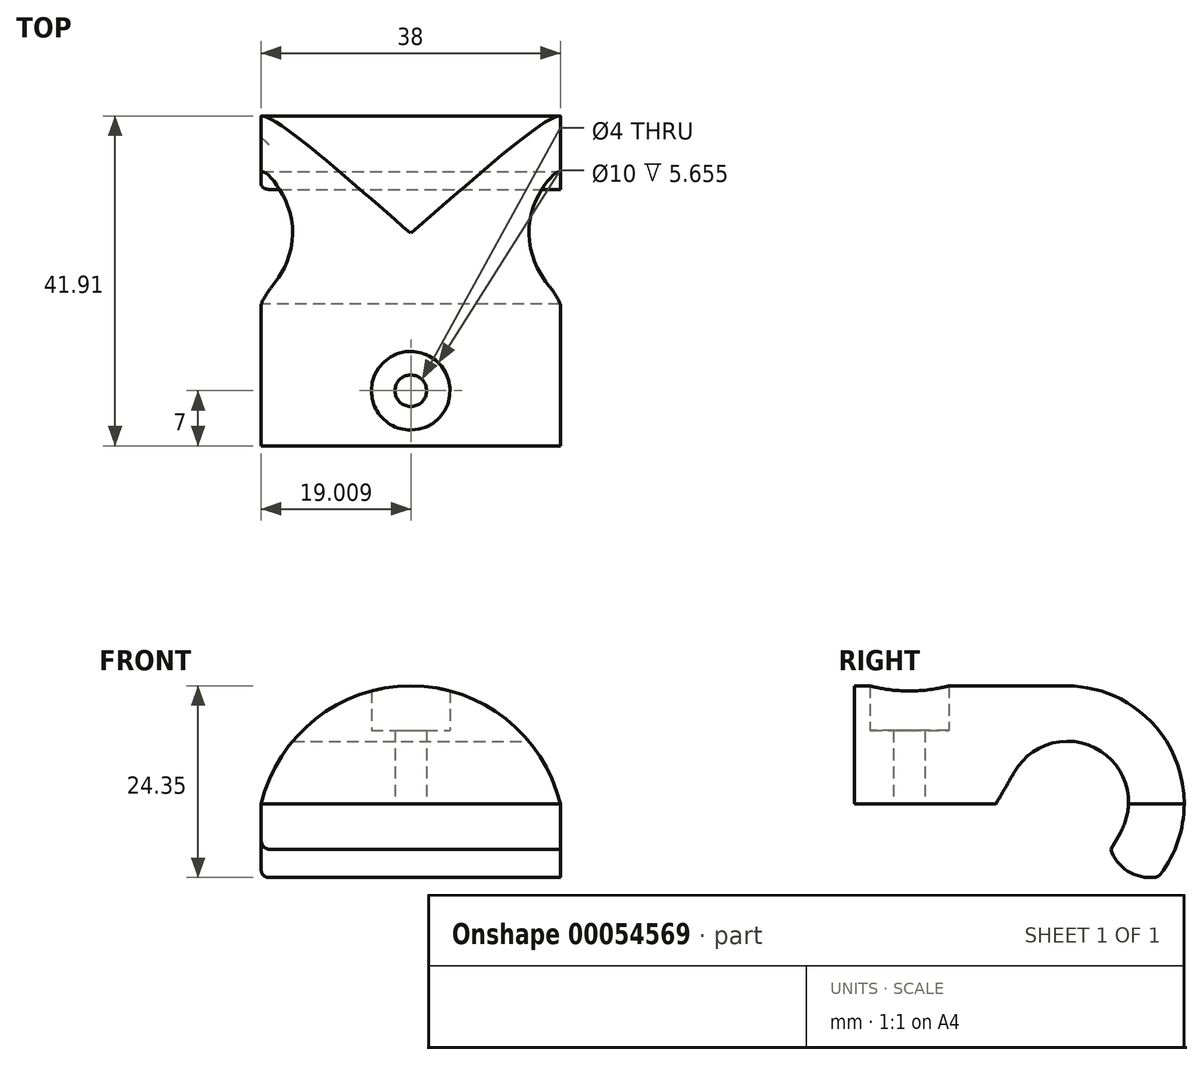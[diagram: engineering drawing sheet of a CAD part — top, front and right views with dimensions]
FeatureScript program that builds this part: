
annotation { "Feature Type Name" : "Feature", "Feature Type Description" : "" }
export const myFeature = defineFeature(function(context is Context, id is Id, definition is map)
    precondition{}
    {
        {
            var Q0;
            Q0=qCreatedBy(makeId("Front.planeOp"),FACE);
            var sketch = newSketch(context, id + "F9", { "sketchPlane" : qUnion([Q0])});
            skLineSegment(sketch, "E0.bottom", {"start": v(38, 0) * mm, "end": v(0, 0) * mm});
            skLineSegment(sketch, "E0.top", {"start": v(38, 29) * mm, "end": v(0, 29) * mm});
            skLineSegment(sketch, "E0.left", {"start": v(38, 29) * mm, "end": v(38, 0) * mm});
            skLineSegment(sketch, "E0.right", {"start": v(0, 29) * mm, "end": v(0, 0) * mm});
            skArc(sketch, "E1", {"start": v(38, 29) * mm, "mid": v(19, 44) * mm, "end": v(0, 29) * mm});
            skSolve(sketch);
        }
        {
            var Q0;
            Q0 = qSketchRegion(id + "F9", true);
            extrude(context, id + "F0", {"entities" : qUnion([Q0]), "oppositeDirection" : true, "depth" : 50 * mm});
        }
        {
            var Q0;
            Q0=makeQuery(id+"F0.opExtrude","SWEPT_FACE",FACE,{"disambiguationData":[OSD([sQuery(id+"F9.wireOp",EDGE,"E0.left")])]});
            var sketch = newSketch(context, id + "F1", { "sketchPlane" : qUnion([Q0])});
            skLineSegment(sketch, "E2", {"start": v(12.87, 20.11) * mm, "end": v(20.37, 33.1) * mm});
            skLineSegment(sketch, "E3", {"start": v(20.37, 33.1) * mm, "end": v(33.8, 25.35) * mm});
            skLineSegment(sketch, "E4", {"start": v(33.8, 25.35) * mm, "end": v(26.3, 12.36) * mm});
            skLineSegment(sketch, "E5", {"start": v(26.3, 12.36) * mm, "end": v(12.87, 20.11) * mm});
            skArc(sketch, "E6", {"start": v(33.8, 25.35) * mm, "mid": v(30.95, 35.94) * mm, "end": v(20.37, 33.1) * mm});
            skArc(sketch, "E7", {"start": v(12.87, 20.11) * mm, "mid": v(15.7, 9.52) * mm, "end": v(26.3, 12.36) * mm});
            skPoint(sketch, "E8", {"position": v(18, 29) * mm});
            skSolve(sketch);
        }
        {
            var Q0;
            Q0 = qSketchRegion(id + "F1", true);
            extrude(context, id + "F2", {"entities" : qUnion([Q0]), "operationType" : NewBodyOperationType.REMOVE, "endBound" : BoundingType.UP_TO_NEXT, "oppositeDirection" : true, "depth" : 25 * mm});
        }
        {
            var Q0;
            Q0=makeQuery(id+"F0.opExtrude","SWEPT_FACE",FACE,{"disambiguationData":[OSD([sQuery(id+"F9.wireOp",EDGE,"E0.left")])]});
            var sketch = newSketch(context, id + "F3", { "sketchPlane" : qUnion([Q0])});
            skPoint(sketch, "E9", {"position": v(26.3, 12.36) * mm});
            skLineSegment(sketch, "E10", {"start": v(38.64, 19.75) * mm, "end": v(38.64, 19.75) * mm});
            skArc(sketch, "E11", {"start": v(32.58, 23.25) * mm, "mid": v(34.95, 20.35) * mm, "end": v(38.64, 19.75) * mm});
            skLineSegment(sketch, "E12", {"start": v(32.58, 23.25) * mm, "end": v(38.64, 19.75) * mm, "construction": true});
            skArc(sketch, "E13", {"start": v(38.64, 19.75) * mm, "mid": v(40.44, 35.54) * mm, "end": v(27, 44) * mm});
            skLineSegment(sketch, "E14", {"start": v(-8.8, 44) * mm, "end": v(55.18, 44) * mm, "construction": true});
            skLineSegment(sketch, "E15", {"start": v(-42.34, 29) * mm, "end": v(32.47, 29) * mm});
            skLineSegment(sketch, "E16", {"start": v(32.47, 29) * mm, "end": v(32.58, 23.25) * mm});
            skLineSegment(sketch, "E17", {"start": v(-42.34, 29) * mm, "end": v(-42.34, -3.9) * mm});
            skLineSegment(sketch, "E18", {"start": v(-42.34, -3.9) * mm, "end": v(62.1, -3.9) * mm});
            skLineSegment(sketch, "E19", {"start": v(62.1, -3.9) * mm, "end": v(62.1, 49.45) * mm});
            skLineSegment(sketch, "E20", {"start": v(62.1, 49.45) * mm, "end": v(25.74, 49.45) * mm});
            skLineSegment(sketch, "E21", {"start": v(25.74, 49.45) * mm, "end": v(27, 44) * mm});
            skSolve(sketch);
        }
        {
            var Q0;
            Q0 = qSketchRegion(id + "F3", true);
            extrude(context, id + "F4", {"entities" : qUnion([Q0]), "operationType" : NewBodyOperationType.REMOVE, "endBound" : BoundingType.THROUGH_ALL, "oppositeDirection" : true, "depth" : 25 * mm});
        }
        {
            var Q0;
            Q0=makeQuery(id+"F4.boolean.opBoolean","COPY",FACE,{"derivedFrom":makeQuery(id+"F4.opExtrude","SWEPT_FACE",FACE,{"disambiguationData":[OSD([sQuery(id+"F3.wireOp",EDGE,"E15")])]})});
            cPlane(context, id + "F5", {"entities" : qUnion([Q0]), "cplaneType" : CPlaneType.OFFSET, "offset" : 15 * mm, "oppositeDirection" : true, "width" : 150 * mm, "height" : 150 * mm});
        }
        {
            var Q0;
            Q0=qCreatedBy(id+"F5.planeOp",FACE);
            var sketch = newSketch(context, id + "F6", { "sketchPlane" : qUnion([Q0])});
            skLineSegment(sketch, "E22", {"start": v(19, -39.67) * mm, "end": v(19, 46.25) * mm, "construction": true});
            skPoint(sketch, "E23", {"position": v(19, 0) * mm});
            skPoint(sketch, "E24", {"position": v(19, -7) * mm});
            skSolve(sketch);
        }
        {
            var Q0;
            Q0=sQuery(id+"F6.wireOp",VERTEX,"E24");
            var Q1;
            Q1=makeQuery(id+"F0.opExtrude","SWEPT_BODY",BODY,{"disambiguationData":[OSD([sQuery(id+"F9.wireOp",EDGE,"E0.bottom"),sQuery(id+"F9.wireOp",EDGE,"E0.left"),sQuery(id+"F9.wireOp",EDGE,"E0.right"),sQuery(id+"F9.wireOp",EDGE,"E1")])]});
            hole(context, id + "F7", {"style" : HoleStyle.C_BORE, "holeDiameter" : 4 * mm, "cBoreDiameter" : 10 * mm, "cBoreDepth" : 5 * mm, "endStyle" : HoleEndStyle.THROUGH, "oppositeDirection" : true, "locations" : qUnion([Q0]), "scope" : qUnion([Q1])});
        }
        {
            var Q0;
            Q0=makeQuery(id+"F4.boolean.opBoolean","COPY",EDGE,{"derivedFrom":makeQuery(id+"F4.opExtrude","SWEPT_EDGE",EDGE,{"disambiguationData":[OSD([sQuery(id+"F3.wireOp",EDGE,"E11"),sQuery(id+"F3.wireOp",EDGE,"E13")])]})});
            var Q1;
            Q1=makeQuery(id+"F4.boolean.opBoolean","COPY",EDGE,{"derivedFrom":makeQuery(id+"F4.opExtrude","CAP_EDGE",EDGE,{"disambiguationData":[OSD([sQuery(id+"F3.wireOp",EDGE,"E11")])],"isStart":true})});
            var Q2;
            Q2=makeQuery(id+"F4.boolean.opBoolean","INTERSECT",EDGE,{"derivedFrom":[makeQuery(id+"F0.opExtrude","SWEPT_FACE",FACE,{"disambiguationData":[OSD([sQuery(id+"F9.wireOp",EDGE,"E0.right")])]}),makeQuery(id+"F4.opExtrude","SWEPT_FACE",FACE,{"disambiguationData":[OSD([sQuery(id+"F3.wireOp",EDGE,"E11")])]})]});
            var Q3;
            Q3=makeQuery(id+"F4.boolean.opBoolean","COPY",EDGE,{"derivedFrom":makeQuery(id+"F4.opExtrude","SWEPT_EDGE",EDGE,{"disambiguationData":[OSD([sQuery(id+"F1.wireOp",EDGE,"E4"),sQuery(id+"F3.wireOp",EDGE,"E11"),sQuery(id+"F3.wireOp",EDGE,"E16")])]})});
            fillet(context, id + "F8", {"entities" : qUnion([Q0, Q1, Q2, Q3]), "radius" : 1 * mm, "tangentPropagation" : true, "allowEdgeOverflow" : false});
        }
    });
